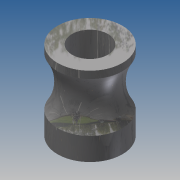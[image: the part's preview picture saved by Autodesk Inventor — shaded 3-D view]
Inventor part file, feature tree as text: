
AUTODESK INVENTOR PART (.ipt)
format: ipt  version: 2015 SP1 (Build 190203100, 203)  size: 148,992 bytes
history: native  units: mm
features: sketch x3, extrude x2, revolve x1, projected_geometry x1
ambient origin geometry x8: Origin, YZ Plane, XZ Plane, XY Plane, X Axis, Y Axis, Z Axis, Center Point
bodies: Volumenkörper1 (feature_tree)
feature tree (7):
  extrude  "Extrusion1"  Depth=11.0mm TaperAngle=0.0deg
  extrude  "Extrusion2"  Depth=11.0mm TaperAngle=0.0deg
  revolve  "Umdrehung1"
  sketch  "Skizze1"  dims[d0=9.0mm d1=11.0mm d2=0.0mm]
  sketch  "Skizze2"  dims[d3=5.0mm d4=11.0mm d5=0.0mm]
  sketch  "Skizze5"  dims[d12=1.0mm d13=5.5mm d14=90.0deg]
  projected_geometry  "Projizierte Kontur2"
